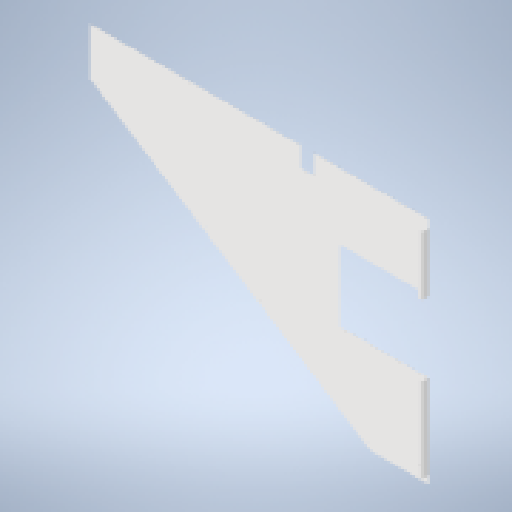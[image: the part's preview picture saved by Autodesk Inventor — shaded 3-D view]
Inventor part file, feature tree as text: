
AUTODESK INVENTOR PART (.ipt)
format: ipt  version: 2025 (Build 290162010, 162A)  size: 483,328 bytes
history: native  units: mm
features: sheet_metal_op x7, sketch x6, extrude x4, other x4, projected_geometry x4, pattern_linear x3, chamfer x1
ambient origin geometry x8: Origin, YZ Plane, XZ Plane, XY Plane, X Axis, Y Axis, Z Axis, Center Point
bodies: Solid1 (feature_tree)
feature tree (29):
  sheet_metal_op  "Face1"
  sheet_metal_op  "Flange1"
  sheet_metal_op  "Flange2"
  extrude  "Extrusion4"  Depth=1420.0mm
  pattern_linear  "Rectangular Pattern6"  Spacing1=41.0mm  [1 undecoded]
  extrude  "Extrusion5"  Depth=120.0mm
  pattern_linear  "Rectangular Pattern7"  Spacing1=0.8mm  [1 undecoded]
  chamfer  "Corner Round1"
  extrude  "Extrusion6"  Depth=0.8mm
  extrude  "Extrusion7"  Depth=0.8mm
  pattern_linear  "Rectangular Pattern8"  Spacing1=0.4mm  [1 undecoded]
  other  "Plate1"
  sketch  "Sketch5"  dims[d0=2095.0mm d1=1420.0mm]
  other  "Plate2"
  sheet_metal_op  "Bend1"
  sheet_metal_op  "Corner1"
  sketch  "Sketch6"  dims[d2=0.8mm]
  other  "Plate3"
  sheet_metal_op  "Bend2"
  sheet_metal_op  "Corner2"
  sketch  "Sketch8"  dims[d50=0.8mm]
  projected_geometry  "Projected Loop3"
  sketch  "Sketch9"  dims[d51=0.4mm]
  projected_geometry  "Projected Loop4"
  sketch  "Sketch10"  dims[d52=1.6mm]
  projected_geometry  "Projected Loop5"
  sketch  "Sketch11"  dims[d53=0.8mm d54=41.0mm d55=90.0deg d56=0.8mm d57=3.2mm d58=0.8mm d59=0.8mm d60=0.8mm d61=0.4mm d62=1.6mm d63=0.8mm d64=25.0mm d65=14.835299mm d66=0.8mm d67=3.2mm d68=0.8mm d69=0.8mm d80=50.0mm d81=50.0mm d82=5.0mm d83=18.0mm d84=0.8mm d85=0.0mm d86=30.0mm d88=600.0mm d89=10.0mm d90=6.0mm d91=15.0mm d92=0.8mm d93=0.0mm d94=40.0mm d96=600.0mm d97=6.0mm d98=295.0mm d99=360.0mm d100=0.0mm d101=0.0mm d103=570.0mm d104=410.0mm d105=545.0mm d106=10.0mm d107=80.0mm d108=120.0mm d109=710.0mm d110=5.0mm d111=20.0mm d112=30.0mm d113=0.0mm d114=0.0mm d115=60.0mm d117=400.0mm]
  projected_geometry  "Projected Loop6"
  other  "Definition1"
note: 3 required parameter values undecoded (feature->parameter linkage not recoverable at this tier; creation-order binding heuristic only, values carry confidence <= 0.55)
